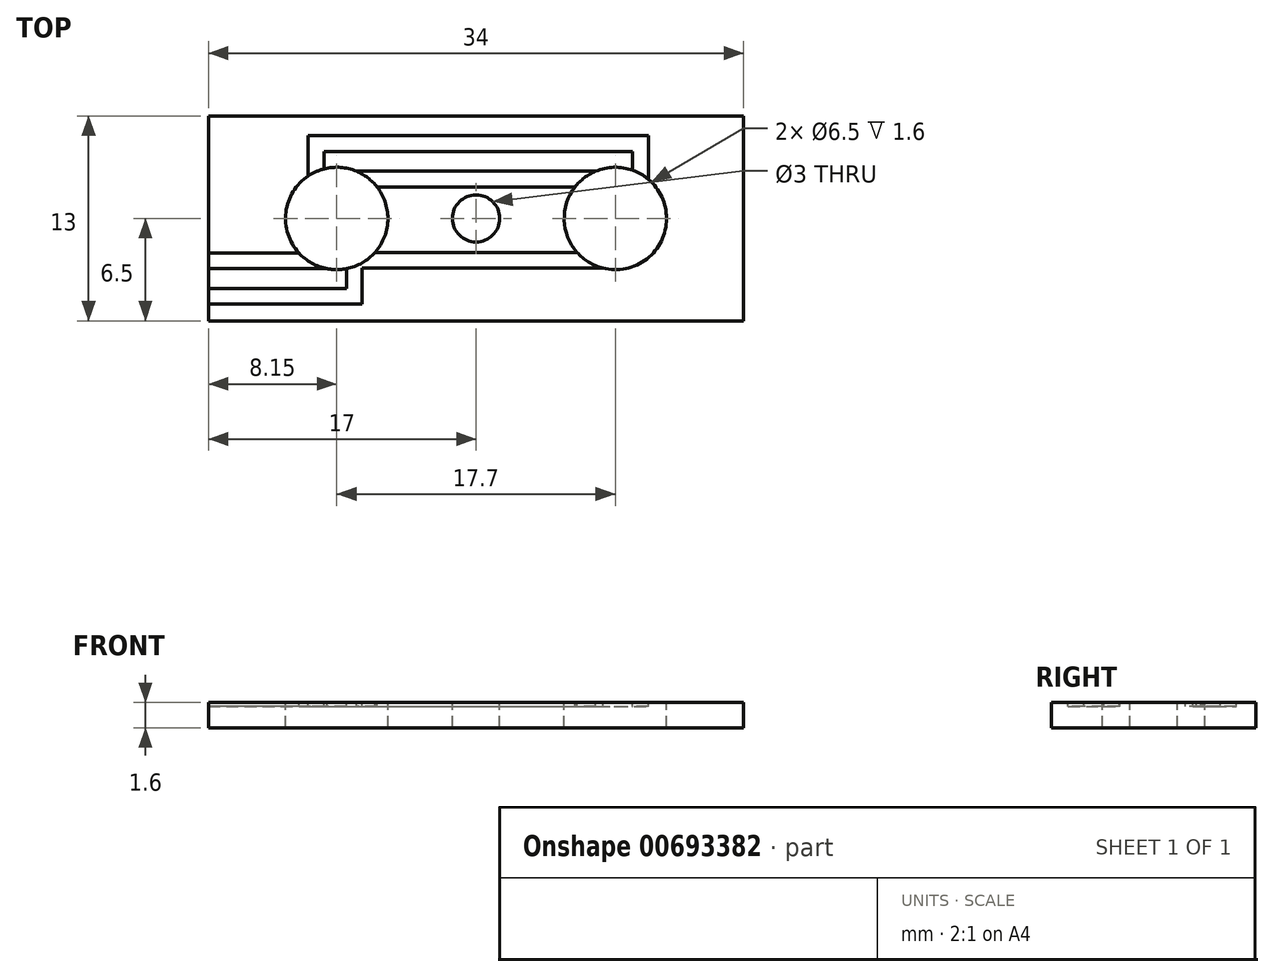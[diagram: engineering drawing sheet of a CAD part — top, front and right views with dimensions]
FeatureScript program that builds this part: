
annotation { "Feature Type Name" : "Feature", "Feature Type Description" : "" }
export const myFeature = defineFeature(function(context is Context, id is Id, definition is map)
    precondition{}
    {
        {
            var Q0;
            Q0=qCreatedBy(makeId("Top.planeOp"),FACE);
            var sketch = newSketch(context, id + "F0", { "sketchPlane" : qUnion([Q0])});
            skLineSegment(sketch, "E0.bottom", {"start": v(-17, 6.5) * mm, "end": v(17, 6.5) * mm});
            skLineSegment(sketch, "E0.top", {"start": v(-17, -6.5) * mm, "end": v(17, -6.5) * mm});
            skLineSegment(sketch, "E0.left", {"start": v(-17, 6.5) * mm, "end": v(-17, -6.5) * mm});
            skLineSegment(sketch, "E0.right", {"start": v(17, 6.5) * mm, "end": v(17, -6.5) * mm});
            skSolve(sketch);
        }
        {
            var Q0;
            Q0=qSketchRegion(id+"F0",true);
            extrude(context, id + "F1", {"entities" : qUnion([Q0]), "depth" : 1.6 * mm, "offsetDistance" : 25 * mm});
        }
        {
            var Q0;
            Q0=makeQuery(id+"F1.opExtrude","CAP_FACE",FACE,{"disambiguationData":[OSD([sQuery(id+"F0.wireOp",EDGE,"E0.bottom"),sQuery(id+"F0.wireOp",EDGE,"E0.top"),sQuery(id+"F0.wireOp",EDGE,"E0.left"),sQuery(id+"F0.wireOp",EDGE,"E0.right")])],"isStart":false});
            var sketch = newSketch(context, id + "F2", { "sketchPlane" : qUnion([Q0])});
            skCircle(sketch, "E1", {"center": v(8.85, 0) * mm, "radius": 3.25 * mm});
            skCircle(sketch, "E2", {"center": v(-8.85, 0) * mm, "radius": 3.25 * mm});
            skCircle(sketch, "E3", {"center": v(0, 0) * mm, "radius": 1.5 * mm});
            skSolve(sketch);
        }
        {
            var Q0;
            Q0=makeQuery(id+"F2.imprint","IMPRINT",FACE,{"disambiguationData":[TD([[makeQuery(id+"F2.imprint","IMPRINT",EDGE,{"derivedFrom":sQuery(id+"F2.wireOp",EDGE,"E2")}),1.0]])]});
            var Q1;
            Q1=makeQuery(id+"F2.imprint","IMPRINT",FACE,{"disambiguationData":[TD([[makeQuery(id+"F2.imprint","IMPRINT",EDGE,{"derivedFrom":sQuery(id+"F2.wireOp",EDGE,"E1")}),1.0]])]});
            extrude(context, id + "F3", {"entities" : qUnion([Q0, Q1]), "operationType" : NewBodyOperationType.REMOVE, "endBound" : BoundingType.THROUGH_ALL, "oppositeDirection" : true, "depth" : 25 * mm, "offsetDistance" : 25 * mm});
        }
        {
            var Q0;
            Q0=makeQuery(id+"F1.opExtrude","CAP_FACE",FACE,{"disambiguationData":[OSD([sQuery(id+"F0.wireOp",EDGE,"E0.bottom"),sQuery(id+"F0.wireOp",EDGE,"E0.top"),sQuery(id+"F0.wireOp",EDGE,"E0.left"),sQuery(id+"F0.wireOp",EDGE,"E0.right")])],"isStart":false});
            var sketch = newSketch(context, id + "F4", { "sketchPlane" : qUnion([Q0])});
            skCircle(sketch, "E4", {"center": v(0, 0) * mm, "radius": 1.5 * mm});
            skSolve(sketch);
        }
        {
            var Q0;
            Q0=makeQuery(id+"F4.imprint","IMPRINT",FACE,{"disambiguationData":[TD([[makeQuery(id+"F4.imprint","IMPRINT",EDGE,{"derivedFrom":sQuery(id+"F4.wireOp",EDGE,"E4")}),1.0]])]});
            extrude(context, id + "F5", {"entities" : qUnion([Q0]), "operationType" : NewBodyOperationType.REMOVE, "endBound" : BoundingType.THROUGH_ALL, "oppositeDirection" : true, "depth" : 25 * mm, "offsetDistance" : 25 * mm});
        }
        {
            var Q0;
            Q0=makeQuery(id+"F1.opExtrude","CAP_FACE",FACE,{"disambiguationData":[OSD([sQuery(id+"F0.wireOp",EDGE,"E0.bottom"),sQuery(id+"F0.wireOp",EDGE,"E0.top"),sQuery(id+"F0.wireOp",EDGE,"E0.left"),sQuery(id+"F0.wireOp",EDGE,"E0.right")])],"isStart":false});
            var sketch = newSketch(context, id + "F6", { "sketchPlane" : qUnion([Q0])});
            skLineSegment(sketch, "E5", {"start": v(-9.66, 3.15) * mm, "end": v(-9.66, 4.25) * mm});
            skLineSegment(sketch, "E6", {"start": v(-9.66, 4.25) * mm, "end": v(9.95, 4.25) * mm});
            skLineSegment(sketch, "E7", {"start": v(9.95, 4.25) * mm, "end": v(9.95, 3.06) * mm});
            skLineSegment(sketch, "E8", {"start": v(-9.48, -3.19) * mm, "end": v(-17, -3.19) * mm});
            skLineSegment(sketch, "E9", {"start": v(-8.23, -3.19) * mm, "end": v(-8.23, -4.44) * mm});
            skLineSegment(sketch, "E10", {"start": v(-8.23, -4.44) * mm, "end": v(-17, -4.44) * mm});
            skLineSegment(sketch, "E11", {"start": v(-6.61, 2) * mm, "end": v(6.29, 2) * mm});
            skLineSegment(sketch, "E12", {"start": v(-8.4, 3) * mm, "end": v(7.84, 3) * mm});
            skLineSegment(sketch, "E13", {"start": v(-10.66, 2.7) * mm, "end": v(-10.66, 5.25) * mm});
            skLineSegment(sketch, "E14", {"start": v(-10.66, 5.25) * mm, "end": v(10.95, 5.25) * mm});
            skLineSegment(sketch, "E15", {"start": v(10.95, 5.25) * mm, "end": v(10.95, 2.48) * mm});
            skLineSegment(sketch, "E16", {"start": v(-11.25, -2.19) * mm, "end": v(-17, -2.19) * mm});
            skLineSegment(sketch, "E17", {"start": v(-8.4, 3.22) * mm, "end": v(-8.4, 3) * mm});
            skLineSegment(sketch, "E18", {"start": v(-9.48, -3.19) * mm, "end": v(-9.48, -3.19) * mm});
            skLineSegment(sketch, "E19", {"start": v(-17, -5.44) * mm, "end": v(-7.23, -5.44) * mm});
            skLineSegment(sketch, "E20", {"start": v(-7.23, -5.44) * mm, "end": v(-7.23, -2.81) * mm});
            skLineSegment(sketch, "E21", {"start": v(-6.41, -2.15) * mm, "end": v(6.41, -2.15) * mm});
            skLineSegment(sketch, "E22", {"start": v(-7.23, -3.15) * mm, "end": v(8.05, -3.15) * mm});
            skLineSegment(sketch, "E23", {"start": v(7.84, 3.09) * mm, "end": v(7.84, 3) * mm});
            skSolve(sketch);
        }
        {
            var Q0;
            {var subQ2=sQuery(id+"F6.wireOp",EDGE,"E5");Q0=makeQuery(id+"F6.imprint","IMPRINT",FACE,{"disambiguationData":[TD([[makeQuery(id+"F6.imprint","IMPRINT",EDGE,{"derivedFrom":subQ2}),1.0]])]});}
            var Q1;
            {var subQ2=sQuery(id+"F6.wireOp",EDGE,"E11");Q1=makeQuery(id+"F6.imprint","IMPRINT",FACE,{"disambiguationData":[TD([[makeQuery(id+"F6.imprint","IMPRINT",EDGE,{"derivedFrom":subQ2}),1.0]])]});}
            var Q2;
            {var subQ0=sQuery(id+"F6.wireOp",EDGE,"E21");Q2=makeQuery(id+"F6.imprint","IMPRINT",FACE,{"disambiguationData":[TD([[makeQuery(id+"F6.imprint","IMPRINT",EDGE,{"derivedFrom":subQ0}),-1.0]])]});}
            var Q3;
            {var subQ3=sQuery(id+"F6.wireOp",EDGE,"E9");Q3=makeQuery(id+"F6.imprint","IMPRINT",FACE,{"disambiguationData":[TD([[makeQuery(id+"F6.imprint","IMPRINT",EDGE,{"derivedFrom":subQ3}),1.0]])]});}
            var Q4;
            {var subQ0=sQuery(id+"F6.wireOp",EDGE,"E8");Q4=makeQuery(id+"F6.imprint","IMPRINT",FACE,{"disambiguationData":[TD([[makeQuery(id+"F6.imprint","IMPRINT",EDGE,{"derivedFrom":subQ0}),-1.0]])]});}
            extrude(context, id + "F7", {"entities" : qUnion([Q0, Q1, Q2, Q3, Q4]), "operationType" : NewBodyOperationType.REMOVE, "oppositeDirection" : true, "depth" : .25 * mm, "offsetDistance" : 25 * mm});
        }
    });
